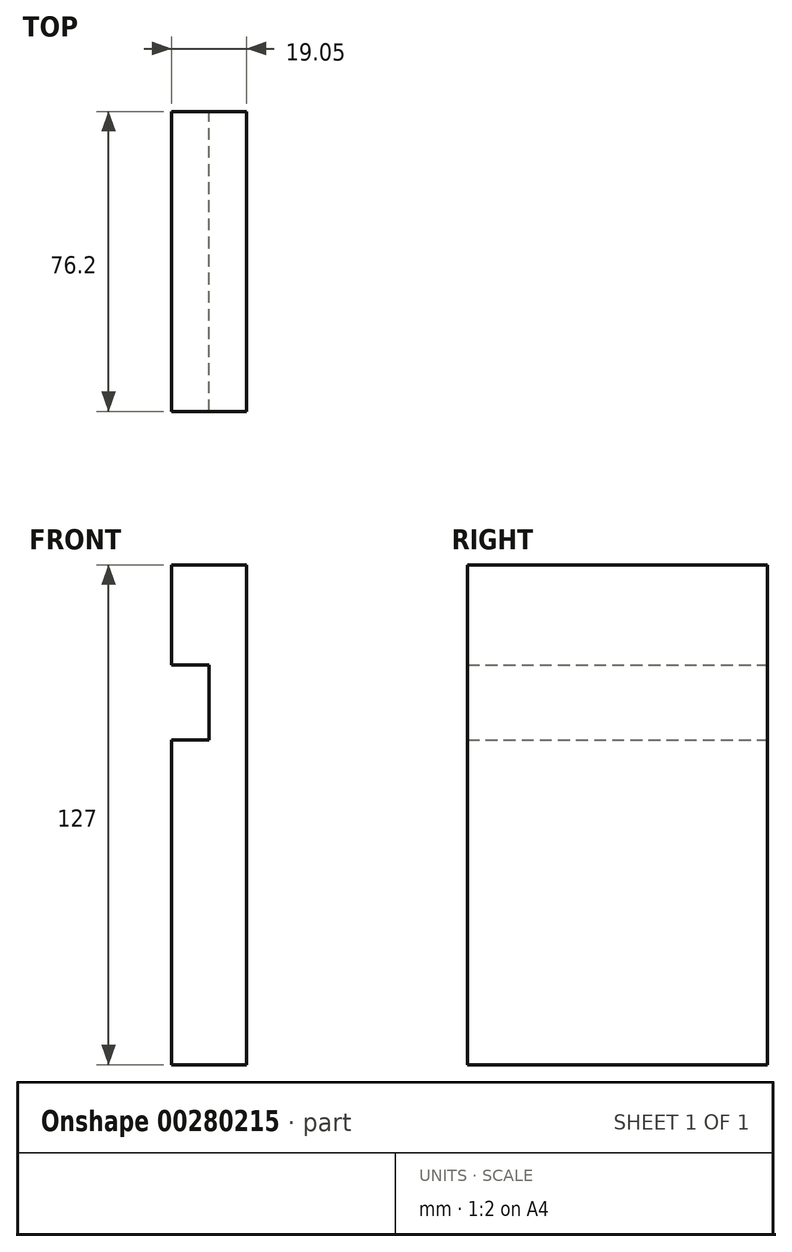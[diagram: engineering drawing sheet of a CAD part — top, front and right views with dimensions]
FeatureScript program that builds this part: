
annotation { "Feature Type Name" : "Feature", "Feature Type Description" : "" }
export const myFeature = defineFeature(function(context is Context, id is Id, definition is map)
    precondition{}
    {
        {
            var Q0;
            Q0=qCreatedBy(makeId("Front.planeOp"),FACE);
            var sketch = newSketch(context, id + "F0", { "sketchPlane" : qUnion([Q0])});
            skLineSegment(sketch, "E0", {"start": v(0, 0) * mm, "end": v(0, 127) * mm});
            skLineSegment(sketch, "E1", {"start": v(0, 127) * mm, "end": v(-19.05, 127) * mm});
            skLineSegment(sketch, "E2", {"start": v(-19.05, 127) * mm, "end": v(-19.05, 101.6) * mm});
            skLineSegment(sketch, "E3", {"start": v(-19.05, 101.6) * mm, "end": v(-9.52, 101.6) * mm});
            skLineSegment(sketch, "E4", {"start": v(-9.52, 101.6) * mm, "end": v(-9.52, 82.55) * mm});
            skLineSegment(sketch, "E5", {"start": v(-9.52, 82.55) * mm, "end": v(-19.05, 82.55) * mm});
            skLineSegment(sketch, "E6", {"start": v(-19.05, 82.55) * mm, "end": v(-19.05, 0) * mm});
            skLineSegment(sketch, "E7", {"start": v(-19.05, 0) * mm, "end": v(0, 0) * mm});
            skSolve(sketch);
        }
        {
            var Q0;
            Q0=qSketchRegion(id+"F0",true);
            extrude(context, id + "F1", {"entities" : qUnion([Q0]), "depth" : 76.2 * mm});
        }
    });
